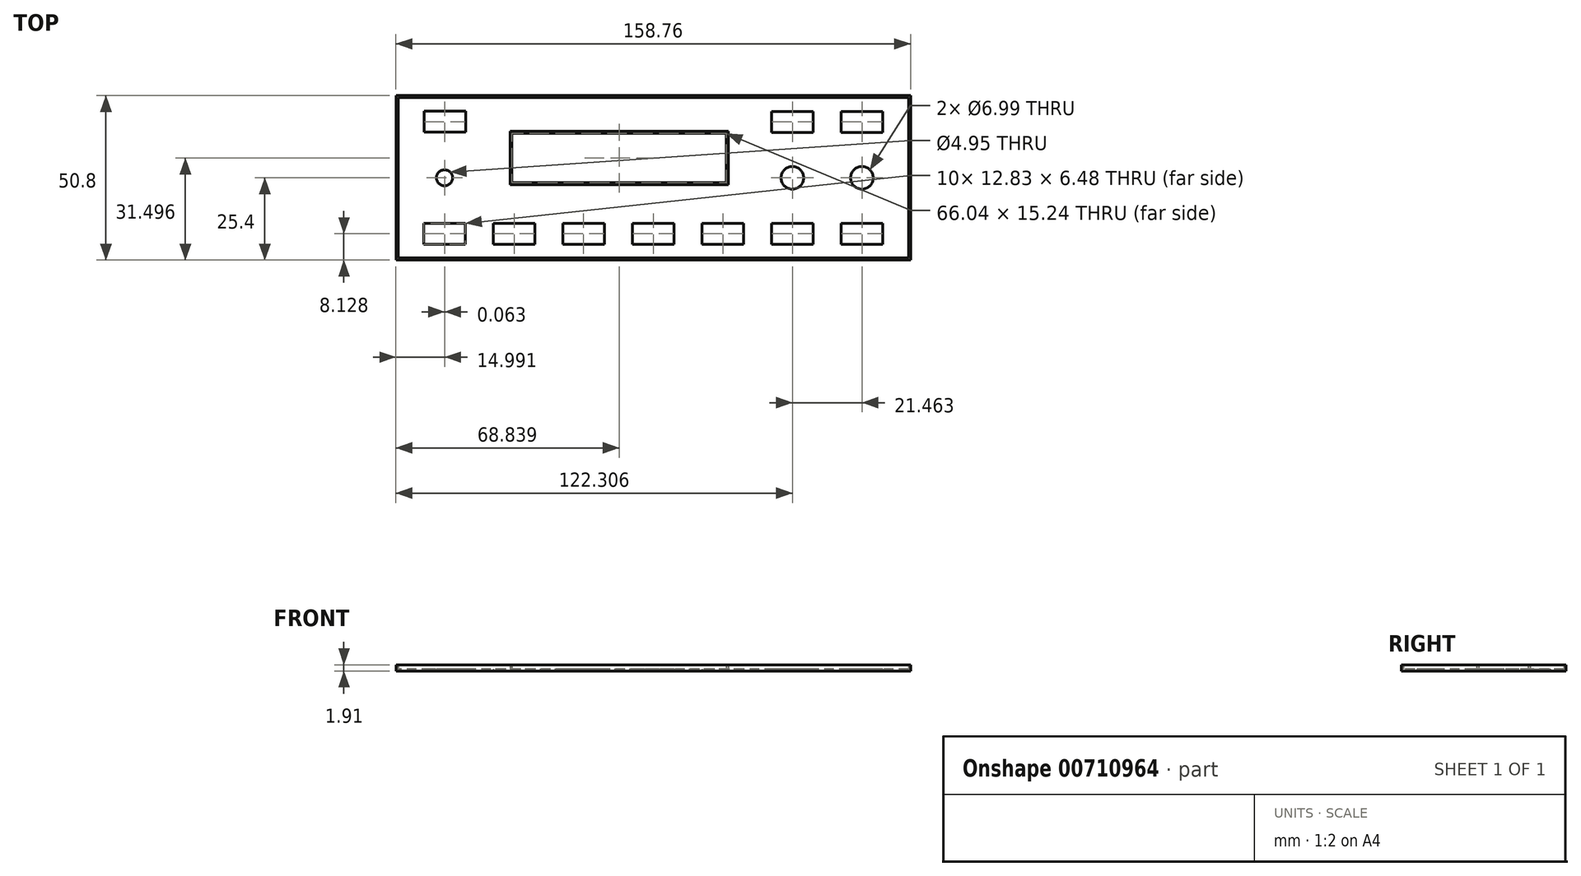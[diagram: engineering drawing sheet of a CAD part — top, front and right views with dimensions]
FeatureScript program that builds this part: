
annotation { "Feature Type Name" : "Feature", "Feature Type Description" : "" }
export const myFeature = defineFeature(function(context is Context, id is Id, definition is map)
    precondition{}
    {
        {
            var Q0;
            Q0=qCreatedBy(makeId("Top.planeOp"),FACE);
            var sketch = newSketch(context, id + "F0", { "sketchPlane" : qUnion([Q0])});
            skLineSegment(sketch, "E0.bottom", {"start": v(79.38, 25.4) * mm, "end": v(-79.38, 25.4) * mm});
            skLineSegment(sketch, "E0.top", {"start": v(79.38, -25.4) * mm, "end": v(-79.38, -25.4) * mm});
            skLineSegment(sketch, "E0.left", {"start": v(79.38, 25.4) * mm, "end": v(79.38, -25.4) * mm});
            skLineSegment(sketch, "E0.right", {"start": v(-79.38, 25.4) * mm, "end": v(-79.38, -25.4) * mm});
            skPoint(sketch, "E0.middle", {"position": v(0, 0) * mm});
            skPoint(sketch, "E1", {"position": v(42.93, 0) * mm});
            skPoint(sketch, "E2", {"position": v(64.39, 0) * mm});
            skLineSegment(sketch, "E3.bottom", {"start": v(49.34, -14.03) * mm, "end": v(36.51, -14.03) * mm});
            skLineSegment(sketch, "E3.top", {"start": v(49.34, -20.51) * mm, "end": v(36.51, -20.51) * mm});
            skLineSegment(sketch, "E3.left", {"start": v(49.34, -14.03) * mm, "end": v(49.34, -20.51) * mm});
            skLineSegment(sketch, "E3.right", {"start": v(36.51, -14.03) * mm, "end": v(36.51, -20.51) * mm});
            skPoint(sketch, "E3.middle", {"position": v(42.93, -17.27) * mm});
            skLineSegment(sketch, "E4.bottom", {"start": v(22.48, -1.52) * mm, "end": v(-43.56, -1.52) * mm});
            skLineSegment(sketch, "E4.top", {"start": v(22.48, 13.72) * mm, "end": v(-43.56, 13.72) * mm});
            skLineSegment(sketch, "E4.left", {"start": v(22.48, -1.52) * mm, "end": v(22.48, 13.72) * mm});
            skLineSegment(sketch, "E4.right", {"start": v(-43.56, -1.52) * mm, "end": v(-43.56, 13.72) * mm});
            skPoint(sketch, "E4.middle", {"position": v(-10.54, 6.1) * mm});
            skLineSegment(sketch, "E5.bottom", {"start": v(-57.91, 14.1) * mm, "end": v(-70.74, 14.1) * mm});
            skLineSegment(sketch, "E5.top", {"start": v(-57.91, 20.57) * mm, "end": v(-70.74, 20.57) * mm});
            skLineSegment(sketch, "E5.left", {"start": v(-57.91, 14.1) * mm, "end": v(-57.91, 20.57) * mm});
            skLineSegment(sketch, "E5.right", {"start": v(-70.74, 14.1) * mm, "end": v(-70.74, 20.57) * mm});
            skPoint(sketch, "E5.middle", {"position": v(-64.33, 17.34) * mm});
            skLineSegment(sketch, "E6.bottom", {"start": v(49.34, 14.03) * mm, "end": v(36.51, 14.03) * mm});
            skLineSegment(sketch, "E6.top", {"start": v(49.34, 20.51) * mm, "end": v(36.51, 20.51) * mm});
            skLineSegment(sketch, "E6.left", {"start": v(49.34, 14.03) * mm, "end": v(49.34, 20.51) * mm});
            skLineSegment(sketch, "E6.right", {"start": v(36.51, 14.03) * mm, "end": v(36.51, 20.51) * mm});
            skPoint(sketch, "E6.middle", {"position": v(42.93, 17.27) * mm});
            skLineSegment(sketch, "E7.bottom", {"start": v(70.8, 14.03) * mm, "end": v(57.98, 14.03) * mm});
            skLineSegment(sketch, "E7.top", {"start": v(70.8, 20.51) * mm, "end": v(57.98, 20.51) * mm});
            skLineSegment(sketch, "E7.left", {"start": v(70.8, 14.03) * mm, "end": v(70.8, 20.51) * mm});
            skLineSegment(sketch, "E7.right", {"start": v(57.98, 14.03) * mm, "end": v(57.98, 20.51) * mm});
            skPoint(sketch, "E7.middle", {"position": v(64.39, 17.27) * mm});
            skLineSegment(sketch, "E8.bottom", {"start": v(27.88, -20.51) * mm, "end": v(15.05, -20.51) * mm});
            skLineSegment(sketch, "E8.top", {"start": v(27.88, -14.03) * mm, "end": v(15.05, -14.03) * mm});
            skLineSegment(sketch, "E8.left", {"start": v(27.88, -20.51) * mm, "end": v(27.88, -14.03) * mm});
            skLineSegment(sketch, "E8.right", {"start": v(15.05, -20.51) * mm, "end": v(15.05, -14.03) * mm});
            skPoint(sketch, "E8.middle", {"position": v(21.46, -17.27) * mm});
            skLineSegment(sketch, "E9.bottom", {"start": v(-57.98, -20.51) * mm, "end": v(-70.8, -20.51) * mm});
            skLineSegment(sketch, "E9.top", {"start": v(-57.98, -14.03) * mm, "end": v(-70.8, -14.03) * mm});
            skLineSegment(sketch, "E9.left", {"start": v(-57.98, -20.51) * mm, "end": v(-57.98, -14.03) * mm});
            skLineSegment(sketch, "E9.right", {"start": v(-70.8, -20.51) * mm, "end": v(-70.8, -14.03) * mm});
            skPoint(sketch, "E9.middle", {"position": v(-64.39, -17.27) * mm});
            skLineSegment(sketch, "E10.bottom", {"start": v(-36.51, -20.51) * mm, "end": v(-49.34, -20.51) * mm});
            skLineSegment(sketch, "E10.top", {"start": v(-36.51, -14.03) * mm, "end": v(-49.34, -14.03) * mm});
            skLineSegment(sketch, "E10.left", {"start": v(-36.51, -20.51) * mm, "end": v(-36.51, -14.03) * mm});
            skLineSegment(sketch, "E10.right", {"start": v(-49.34, -20.51) * mm, "end": v(-49.34, -14.03) * mm});
            skPoint(sketch, "E10.middle", {"position": v(-42.93, -17.27) * mm});
            skLineSegment(sketch, "E11.bottom", {"start": v(-15.05, -20.51) * mm, "end": v(-27.88, -20.51) * mm});
            skLineSegment(sketch, "E11.top", {"start": v(-15.05, -14.03) * mm, "end": v(-27.88, -14.03) * mm});
            skLineSegment(sketch, "E11.left", {"start": v(-15.05, -20.51) * mm, "end": v(-15.05, -14.03) * mm});
            skLineSegment(sketch, "E11.right", {"start": v(-27.88, -20.51) * mm, "end": v(-27.88, -14.03) * mm});
            skPoint(sketch, "E11.middle", {"position": v(-21.46, -17.27) * mm});
            skLineSegment(sketch, "E12.bottom", {"start": v(6.41, -20.51) * mm, "end": v(-6.41, -20.51) * mm});
            skLineSegment(sketch, "E12.top", {"start": v(6.41, -14.03) * mm, "end": v(-6.41, -14.03) * mm});
            skLineSegment(sketch, "E12.left", {"start": v(6.41, -20.51) * mm, "end": v(6.41, -14.03) * mm});
            skLineSegment(sketch, "E12.right", {"start": v(-6.41, -20.51) * mm, "end": v(-6.41, -14.03) * mm});
            skPoint(sketch, "E12.middle", {"position": v(0, -17.27) * mm});
            skLineSegment(sketch, "E13.bottom", {"start": v(70.8, -20.51) * mm, "end": v(57.98, -20.51) * mm});
            skLineSegment(sketch, "E13.top", {"start": v(70.8, -14.03) * mm, "end": v(57.98, -14.03) * mm});
            skLineSegment(sketch, "E13.left", {"start": v(70.8, -20.51) * mm, "end": v(70.8, -14.03) * mm});
            skLineSegment(sketch, "E13.right", {"start": v(57.98, -20.51) * mm, "end": v(57.98, -14.03) * mm});
            skPoint(sketch, "E13.middle", {"position": v(64.39, -17.27) * mm});
            skPoint(sketch, "E14", {"position": v(-64.39, 0) * mm});
            skSolve(sketch);
        }
        {
            var Q0;
            Q0=makeQuery(id+"F0.imprint","IMPRINT",FACE,{"disambiguationData":[TD([[makeQuery(id+"F0.imprint","IMPRINT",EDGE,{"derivedFrom":sQuery(id+"F0.wireOp",EDGE,"E0.bottom")}),1.0]])]});
            extrude(context, id + "F1", {"entities" : qUnion([Q0]), "depth" : 0.64 * mm, "offsetDistance" : 25.4 * mm});
        }
        {
            var Q0;
            Q0=sQuery(id+"F0.wireOp",VERTEX,"E1");
            var Q1;
            Q1=makeQuery(id+"F1.opExtrude","SWEPT_BODY",BODY,{"disambiguationData":[OSD([sQuery(id+"F0.wireOp",EDGE,"E0.bottom"),sQuery(id+"F0.wireOp",EDGE,"E0.top"),sQuery(id+"F0.wireOp",EDGE,"E0.left"),sQuery(id+"F0.wireOp",EDGE,"E0.right"),sQuery(id+"F0.wireOp",EDGE,"YCmz3xOG-VUtS-z0pb-juDh-28fmZs25sxiE.bottom"),sQuery(id+"F0.wireOp",EDGE,"YCmz3xOG-VUtS-z0pb-juDh-28fmZs25sxiE.top"),sQuery(id+"F0.wireOp",EDGE,"YCmz3xOG-VUtS-z0pb-juDh-28fmZs25sxiE.left"),sQuery(id+"F0.wireOp",EDGE,"YCmz3xOG-VUtS-z0pb-juDh-28fmZs25sxiE.right")])]});
            hole(context, id + "F2", {"style" : HoleStyle.SIMPLE, "endStyle" : HoleEndStyle.THROUGH, "oppositeDirection" : true, "holeDiameter" : 7 * mm, "majorDiameter" : 6.35 * mm, "isTappedThrough" : true, "tappedDepth" : 12.7 * mm, "tapClearance" : 3, "locations" : qUnion([Q0]), "scope" : qUnion([Q1])});
        }
        {
            var Q0;
            Q0=sQuery(id+"F0.wireOp",VERTEX,"E2");
            var Q1;
            Q1=makeQuery(id+"F1.opExtrude","SWEPT_BODY",BODY,{"disambiguationData":[OSD([sQuery(id+"F0.wireOp",EDGE,"E0.bottom"),sQuery(id+"F0.wireOp",EDGE,"E0.top"),sQuery(id+"F0.wireOp",EDGE,"E0.left"),sQuery(id+"F0.wireOp",EDGE,"E0.right"),sQuery(id+"F0.wireOp",EDGE,"YCmz3xOG-VUtS-z0pb-juDh-28fmZs25sxiE.bottom"),sQuery(id+"F0.wireOp",EDGE,"YCmz3xOG-VUtS-z0pb-juDh-28fmZs25sxiE.top"),sQuery(id+"F0.wireOp",EDGE,"YCmz3xOG-VUtS-z0pb-juDh-28fmZs25sxiE.left"),sQuery(id+"F0.wireOp",EDGE,"YCmz3xOG-VUtS-z0pb-juDh-28fmZs25sxiE.right")])]});
            hole(context, id + "F3", {"style" : HoleStyle.SIMPLE, "endStyle" : HoleEndStyle.THROUGH, "oppositeDirection" : true, "holeDiameter" : 7 * mm, "majorDiameter" : 6.35 * mm, "isTappedThrough" : true, "tappedDepth" : 12.7 * mm, "tapClearance" : 3, "locations" : qUnion([Q0]), "scope" : qUnion([Q1])});
        }
        {
            var Q0;
            Q0=qCreatedBy(makeId("Top.planeOp"),FACE);
            cPlane(context, id + "F4", {"entities" : qUnion([Q0]), "cplaneType" : CPlaneType.OFFSET, "offset" : 0.64 * mm, "width" : 152.4 * mm, "height" : 152.4 * mm});
        }
        {
            var Q0;
            Q0=qCreatedBy(id+"F4.planeOp",FACE);
            var sketch = newSketch(context, id + "F5", { "sketchPlane" : qUnion([Q0])});
            skLineSegment(sketch, "E15.bottom", {"start": v(79.38, 25.4) * mm, "end": v(-79.38, 25.4) * mm});
            skLineSegment(sketch, "E15.top", {"start": v(79.38, -25.4) * mm, "end": v(-79.38, -25.4) * mm});
            skLineSegment(sketch, "E15.left", {"start": v(79.38, 25.4) * mm, "end": v(79.38, -25.4) * mm});
            skLineSegment(sketch, "E15.right", {"start": v(-79.38, 25.4) * mm, "end": v(-79.38, -25.4) * mm});
            skPoint(sketch, "E15.middle", {"position": v(0, 0) * mm});
            skLineSegment(sketch, "E16.bottom", {"start": v(78.74, 24.77) * mm, "end": v(-78.74, 24.77) * mm});
            skLineSegment(sketch, "E16.top", {"start": v(78.74, -24.77) * mm, "end": v(-78.74, -24.77) * mm});
            skLineSegment(sketch, "E16.left", {"start": v(78.74, 24.77) * mm, "end": v(78.74, -24.77) * mm});
            skLineSegment(sketch, "E16.right", {"start": v(-78.74, 24.77) * mm, "end": v(-78.74, -24.77) * mm});
            skSolve(sketch);
        }
        {
            var Q0;
            Q0=qSketchRegion(id+"F5",true);
            extrude(context, id + "F6", {"entities" : qUnion([Q0]), "operationType" : NewBodyOperationType.ADD, "depth" : 1.27 * mm, "offsetDistance" : 25.4 * mm});
        }
        {
            var Q0;
            Q0=qCreatedBy(id+"F4.planeOp",FACE);
            var sketch = newSketch(context, id + "F7", { "sketchPlane" : qUnion([Q0])});
            skPoint(sketch, "E17.middle", {"position": v(0, 0) * mm});
            skLineSegment(sketch, "E18.bottom", {"start": v(-43.56, 13.72) * mm, "end": v(22.48, 13.72) * mm});
            skLineSegment(sketch, "E18.top", {"start": v(-43.56, -1.52) * mm, "end": v(22.48, -1.52) * mm});
            skLineSegment(sketch, "E18.left", {"start": v(-43.56, 13.72) * mm, "end": v(-43.56, -1.52) * mm});
            skLineSegment(sketch, "E18.right", {"start": v(22.48, 13.72) * mm, "end": v(22.48, -1.52) * mm});
            skLineSegment(sketch, "E19.bottom", {"start": v(-44.2, 14.35) * mm, "end": v(23.11, 14.35) * mm});
            skLineSegment(sketch, "E19.top", {"start": v(-44.2, -2.16) * mm, "end": v(23.11, -2.16) * mm});
            skLineSegment(sketch, "E19.left", {"start": v(-44.2, 14.35) * mm, "end": v(-44.2, -2.16) * mm});
            skLineSegment(sketch, "E19.right", {"start": v(23.11, 14.35) * mm, "end": v(23.11, -2.16) * mm});
            skSolve(sketch);
        }
        {
            var Q0;
            Q0=qSketchRegion(id+"F7",true);
            extrude(context, id + "F8", {"entities" : qUnion([Q0]), "operationType" : NewBodyOperationType.ADD, "depth" : 1.27 * mm, "offsetDistance" : 25.4 * mm});
        }
        {
            var Q0;
            Q0=sQuery(id+"F0.wireOp",VERTEX,"E14");
            var Q1;
            Q1=makeQuery(id+"F1.opExtrude","SWEPT_BODY",BODY,{"disambiguationData":[OSD([sQuery(id+"F0.wireOp",EDGE,"E0.bottom"),sQuery(id+"F0.wireOp",EDGE,"E0.top"),sQuery(id+"F0.wireOp",EDGE,"E0.left"),sQuery(id+"F0.wireOp",EDGE,"E0.right"),sQuery(id+"F0.wireOp",EDGE,"E3.bottom"),sQuery(id+"F0.wireOp",EDGE,"E3.top"),sQuery(id+"F0.wireOp",EDGE,"E3.left"),sQuery(id+"F0.wireOp",EDGE,"E3.right"),sQuery(id+"F0.wireOp",EDGE,"E4.bottom"),sQuery(id+"F0.wireOp",EDGE,"E4.top"),sQuery(id+"F0.wireOp",EDGE,"E4.left"),sQuery(id+"F0.wireOp",EDGE,"E4.right"),sQuery(id+"F0.wireOp",EDGE,"E5.bottom"),sQuery(id+"F0.wireOp",EDGE,"E5.top"),sQuery(id+"F0.wireOp",EDGE,"E5.left"),sQuery(id+"F0.wireOp",EDGE,"E5.right"),sQuery(id+"F0.wireOp",EDGE,"E6.bottom"),sQuery(id+"F0.wireOp",EDGE,"E6.top"),sQuery(id+"F0.wireOp",EDGE,"E6.left"),sQuery(id+"F0.wireOp",EDGE,"E6.right"),sQuery(id+"F0.wireOp",EDGE,"E7.bottom"),sQuery(id+"F0.wireOp",EDGE,"E7.top"),sQuery(id+"F0.wireOp",EDGE,"E7.left"),sQuery(id+"F0.wireOp",EDGE,"E7.right"),sQuery(id+"F0.wireOp",EDGE,"E8.bottom"),sQuery(id+"F0.wireOp",EDGE,"E8.top"),sQuery(id+"F0.wireOp",EDGE,"E8.left"),sQuery(id+"F0.wireOp",EDGE,"E8.right"),sQuery(id+"F0.wireOp",EDGE,"E9.bottom"),sQuery(id+"F0.wireOp",EDGE,"E9.top"),sQuery(id+"F0.wireOp",EDGE,"E9.left"),sQuery(id+"F0.wireOp",EDGE,"E9.right"),sQuery(id+"F0.wireOp",EDGE,"E10.bottom"),sQuery(id+"F0.wireOp",EDGE,"E10.top"),sQuery(id+"F0.wireOp",EDGE,"E10.left"),sQuery(id+"F0.wireOp",EDGE,"E10.right"),sQuery(id+"F0.wireOp",EDGE,"E11.bottom"),sQuery(id+"F0.wireOp",EDGE,"E11.top"),sQuery(id+"F0.wireOp",EDGE,"E11.left"),sQuery(id+"F0.wireOp",EDGE,"E11.right"),sQuery(id+"F0.wireOp",EDGE,"E12.bottom"),sQuery(id+"F0.wireOp",EDGE,"E12.top"),sQuery(id+"F0.wireOp",EDGE,"E12.left"),sQuery(id+"F0.wireOp",EDGE,"E12.right"),sQuery(id+"F0.wireOp",EDGE,"E13.bottom"),sQuery(id+"F0.wireOp",EDGE,"E13.top"),sQuery(id+"F0.wireOp",EDGE,"E13.left"),sQuery(id+"F0.wireOp",EDGE,"E13.right")])]});
            hole(context, id + "F9", {"style" : HoleStyle.SIMPLE, "endStyle" : HoleEndStyle.THROUGH, "oppositeDirection" : true, "holeDiameter" : 4.95 * mm, "majorDiameter" : 6.35 * mm, "isTappedThrough" : true, "tappedDepth" : 12.7 * mm, "tapClearance" : 3, "locations" : qUnion([Q0]), "scope" : qUnion([Q1])});
        }
    });
